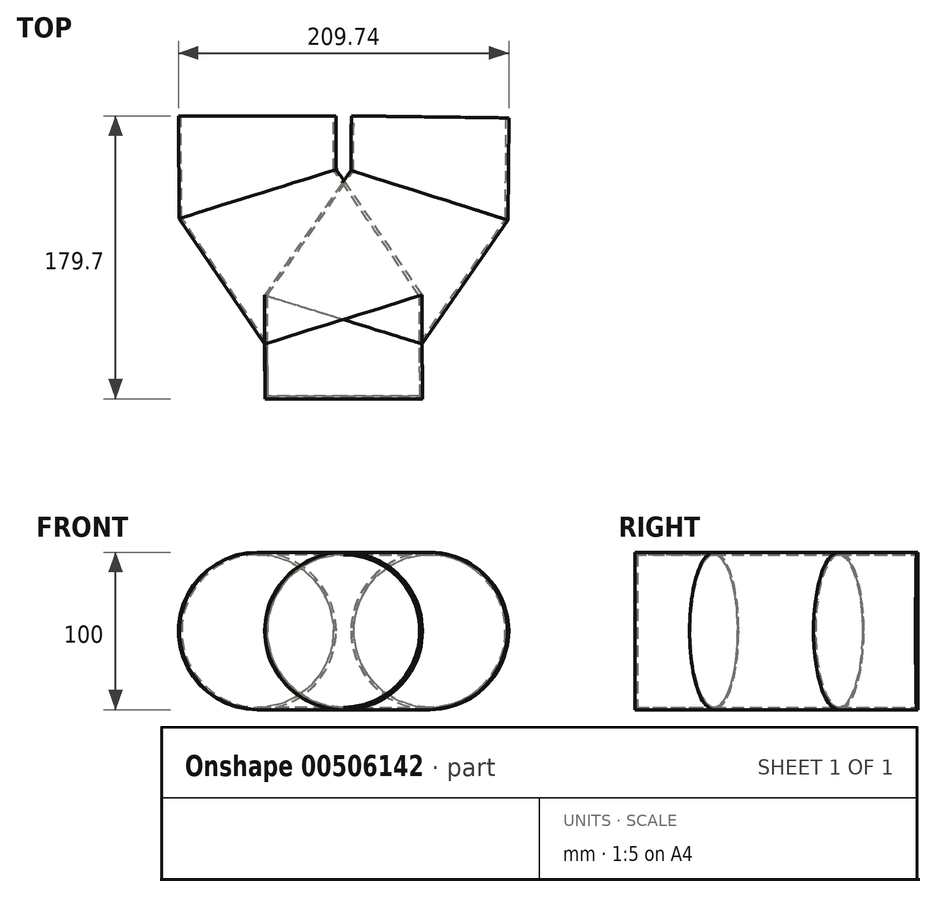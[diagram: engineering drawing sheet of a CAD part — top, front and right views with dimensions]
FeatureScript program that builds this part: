
annotation { "Feature Type Name" : "Feature", "Feature Type Description" : "" }
export const myFeature = defineFeature(function(context is Context, id is Id, definition is map)
    precondition{}
    {
        {
            var Q0;
            Q0=qCreatedBy(makeId("Top.planeOp"),FACE);
            var sketch = newSketch(context, id + "F0", { "sketchPlane" : qUnion([Q0])});
            skLineSegment(sketch, "E0", {"start": v(54.31, 129.32) * mm, "end": v(54.7, 179.31) * mm});
            skLineSegment(sketch, "E1", {"start": v(-54.77, 130) * mm, "end": v(-55.04, 180) * mm});
            skLineSegment(sketch, "E2", {"start": v(-0.14, 0.3) * mm, "end": v(-0.41, 50.3) * mm});
            skLineSegment(sketch, "E3", {"start": v(-0.41, 50.3) * mm, "end": v(-54.77, 130) * mm});
            skLineSegment(sketch, "E4", {"start": v(-0.41, 50.3) * mm, "end": v(54.31, 129.32) * mm});
            skSolve(sketch);
        }
        {
            var Q0;
            Q0=qCreatedBy(makeId("Front.planeOp"),FACE);
            var sketch = newSketch(context, id + "F1", { "sketchPlane" : qUnion([Q0])});
            skCircle(sketch, "E5", {"center": v(0, 0) * mm, "radius": 50 * mm});
            skSolve(sketch);
        }
        {
            var Q0;
            Q0=makeQuery(id+"F1.imprint","IMPRINT",FACE,{"disambiguationData":[TD([[makeQuery(id+"F1.imprint","IMPRINT",EDGE,{"derivedFrom":sQuery(id+"F1.wireOp",EDGE,"E5")}),1.0]])]});
            var Q1;
            Q1=sQuery(id+"F0.wireOp",EDGE,"E2");
            var Q2;
            Q2=sQuery(id+"F0.wireOp",EDGE,"E3");
            var Q3;
            Q3=sQuery(id+"F0.wireOp",EDGE,"E1");
            sweep(context, id + "F2", {"profiles" : qUnion([Q0]), "path" : qUnion([Q1, Q2, Q3])});
        }
        {
            var Q0;
            Q0=makeQuery(id+"F1.imprint","IMPRINT",FACE,{"disambiguationData":[TD([[makeQuery(id+"F1.imprint","IMPRINT",EDGE,{"derivedFrom":sQuery(id+"F1.wireOp",EDGE,"E5")}),1.0]])]});
            var Q1;
            Q1=sQuery(id+"F0.wireOp",EDGE,"E2");
            var Q2;
            Q2=sQuery(id+"F0.wireOp",EDGE,"E4");
            var Q3;
            Q3=sQuery(id+"F0.wireOp",EDGE,"E0");
            sweep(context, id + "F3", {"profiles" : qUnion([Q0]), "path" : qUnion([Q1, Q2, Q3])});
        }
        {
            var Q0;
            Q0=makeQuery(id+"F3.opSweep","CAP_FACE",FACE,{"disambiguationData":[OSD([sQuery(id+"F0.wireOp",VERTEX,"E2.start"),sQuery(id+"F1.wireOp",EDGE,"E5")])],"isStart":true});
            var Q1;
            Q1=makeQuery(id+"F3.opSweep","CAP_FACE",FACE,{"disambiguationData":[OSD([sQuery(id+"F0.wireOp",VERTEX,"E0.end"),sQuery(id+"F1.wireOp",EDGE,"E5")])],"isStart":false});
            var Q2;
            Q2=makeQuery(id+"F2.opSweep","CAP_FACE",FACE,{"disambiguationData":[OSD([sQuery(id+"F0.wireOp",VERTEX,"E1.end"),sQuery(id+"F1.wireOp",EDGE,"E5")])],"isStart":false});
            shell(context, id + "F4", {"entities" : qUnion([Q0, Q1, Q2]), "thickness" : 1.6 * mm});
        }
    });
